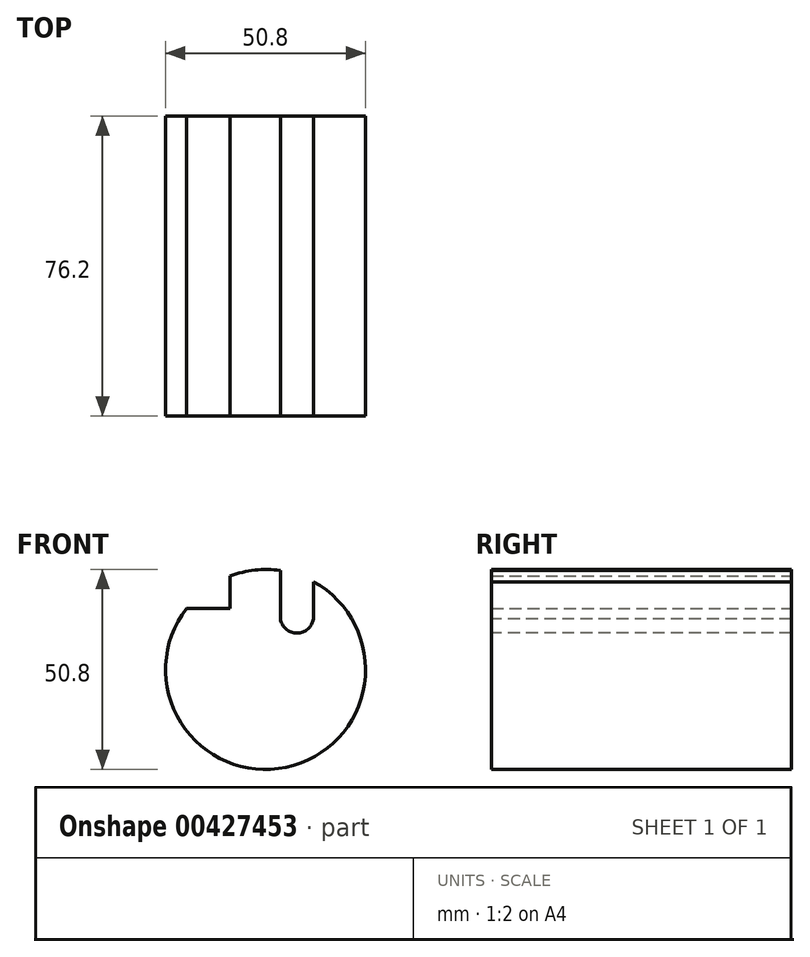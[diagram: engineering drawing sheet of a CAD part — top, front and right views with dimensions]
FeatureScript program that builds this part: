
annotation { "Feature Type Name" : "Feature", "Feature Type Description" : "" }
export const myFeature = defineFeature(function(context is Context, id is Id, definition is map)
    precondition{}
    {
        {
            var Q0;
            Q0=qCreatedBy(makeId("Front.planeOp"),FACE);
            var sketch = newSketch(context, id + "F0", { "sketchPlane" : qUnion([Q0])});
            skCircle(sketch, "E0", {"center": v(0, 0) * mm, "radius": 25.4 * mm});
            skSolve(sketch);
        }
        {
            var Q0;
            Q0=makeQuery(id+"F0.imprint","IMPRINT",FACE,{"disambiguationData":[TD([[makeQuery(id+"F0.imprint","IMPRINT",EDGE,{"derivedFrom":sQuery(id+"F0.wireOp",EDGE,"E0")}),1.0]])]});
            extrude(context, id + "F1", {"entities" : qUnion([Q0]), "depth" : 76.2 * mm});
        }
        {
            var Q0;
            Q0=makeQuery(id+"F1.opExtrude","CAP_FACE",FACE,{"disambiguationData":[OSD([sQuery(id+"F0.wireOp",EDGE,"E0")])],"isStart":false});
            var sketch = newSketch(context, id + "F2", { "sketchPlane" : qUnion([Q0])});
            skLineSegment(sketch, "E1.bottom", {"start": v(-9, 15.5) * mm, "end": v(-29.57, 15.5) * mm});
            skLineSegment(sketch, "E1.top", {"start": v(-9, 27.78) * mm, "end": v(-29.57, 27.78) * mm});
            skLineSegment(sketch, "E1.left", {"start": v(-9, 15.5) * mm, "end": v(-9, 27.78) * mm});
            skLineSegment(sketch, "E1.right", {"start": v(-29.57, 15.5) * mm, "end": v(-29.57, 27.78) * mm});
            skSolve(sketch);
        }
        {
            var Q0;
            Q0 = qSketchRegion(id + "F2", true);
            extrude(context, id + "F3", {"entities" : qUnion([Q0]), "operationType" : NewBodyOperationType.REMOVE, "oppositeDirection" : true, "depth" : 76.2 * mm});
        }
        {
            var Q0;
            Q0=makeQuery(id+"F1.opExtrude","CAP_FACE",FACE,{"disambiguationData":[OSD([sQuery(id+"F0.wireOp",EDGE,"E0")])],"isStart":false});
            var sketch = newSketch(context, id + "F4", { "sketchPlane" : qUnion([Q0])});
            skLineSegment(sketch, "E2.bottom", {"start": v(3.78, 12.87) * mm, "end": v(12.17, 12.87) * mm});
            skLineSegment(sketch, "E2.top", {"start": v(3.78, 36.09) * mm, "end": v(12.17, 36.09) * mm});
            skLineSegment(sketch, "E2.left", {"start": v(3.78, 12.87) * mm, "end": v(3.78, 36.09) * mm});
            skLineSegment(sketch, "E2.right", {"start": v(12.17, 12.87) * mm, "end": v(12.17, 36.09) * mm});
            skCircle(sketch, "E3", {"center": v(7.97, 13.47) * mm, "radius": 4.24 * mm});
            skPoint(sketch, "E3.third.point", {"position": v(7.97, 9.23) * mm});
            skPoint(sketch, "E3.third.point.positionSnap0", {"position": v(7.97, 12.87) * mm});
            skSolve(sketch);
        }
        {
            var Q0;
            {var subQ0=sQuery(id+"F4.wireOp",EDGE,"E2.bottom");Q0=makeQuery(id+"F4.imprint","IMPRINT",FACE,{"disambiguationData":[TD([[makeQuery(id+"F4.imprint","IMPRINT",EDGE,{"derivedFrom":subQ0}),-1.0]])]});}
            var Q1;
            {var subQ0=sQuery(id+"F4.wireOp",EDGE,"E2.bottom");Q1=makeQuery(id+"F4.imprint","IMPRINT",FACE,{"disambiguationData":[TD([[makeQuery(id+"F4.imprint","IMPRINT",EDGE,{"derivedFrom":subQ0}),1.0]])]});}
            var Q2;
            {var subQ0=sQuery(id+"F4.wireOp",EDGE,"E2.top");Q2=makeQuery(id+"F4.imprint","IMPRINT",FACE,{"disambiguationData":[TD([[makeQuery(id+"F4.imprint","IMPRINT",EDGE,{"derivedFrom":subQ0}),-1.0]])]});}
            var Q3;
            {var subQ0=sQuery(id+"F4.wireOp",EDGE,"E3");var subQ1=sQuery(id+"F4.wireOp",EDGE,"E2.left");var subQ2=makeQuery(id+"F4.imprint","INTERSECT",VERTEX,{"derivedFrom":[subQ1,subQ0]});Q3=makeQuery(id+"F4.imprint","IMPRINT",FACE,{"disambiguationData":[TD([[makeQuery(id+"F4.imprint","IMPRINT",EDGE,{"disambiguationData":[TD([[subQ2,-1.0]])],"derivedFrom":subQ1}),-1.0]])]});}
            extrude(context, id + "F5", {"entities" : qUnion([Q0, Q1, Q2, Q3]), "operationType" : NewBodyOperationType.REMOVE, "oppositeDirection" : true, "depth" : 76.2 * mm});
        }
    });
